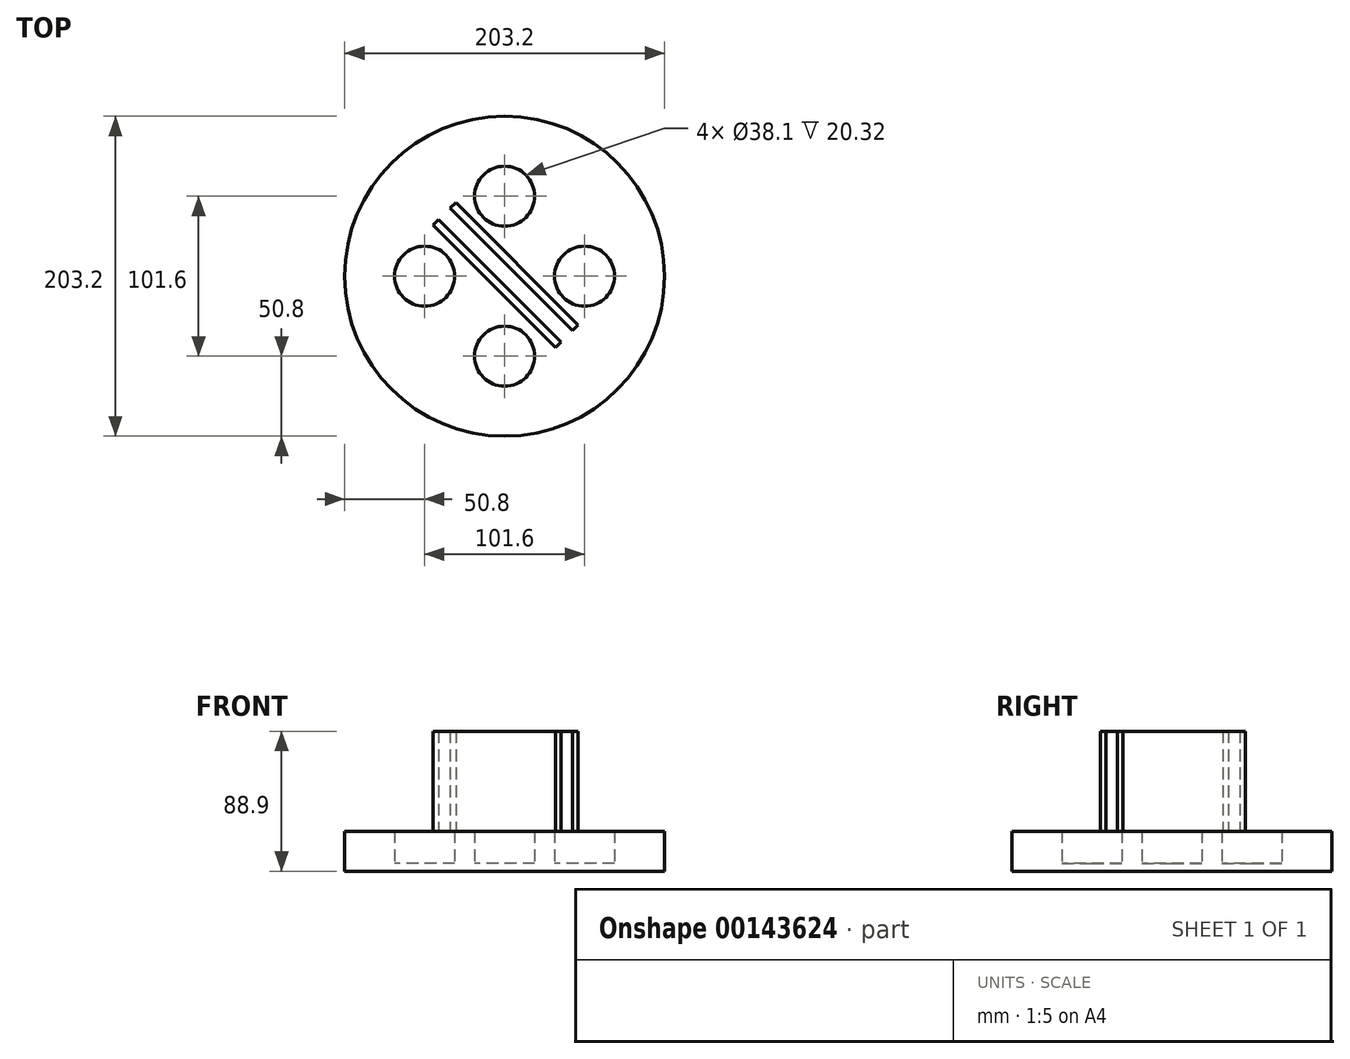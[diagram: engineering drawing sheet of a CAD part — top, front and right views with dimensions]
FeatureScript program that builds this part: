
annotation { "Feature Type Name" : "Feature", "Feature Type Description" : "" }
export const myFeature = defineFeature(function(context is Context, id is Id, definition is map)
    precondition{}
    {
        {
            var Q0;
            Q0=qCreatedBy(makeId("Top.planeOp"),FACE);
            var sketch = newSketch(context, id + "F0", { "sketchPlane" : qUnion([Q0])});
            skCircle(sketch, "E0", {"center": v(0, 0) * mm, "radius": 101.6 * mm});
            skLineSegment(sketch, "E1", {"start": v(0, 0) * mm, "end": v(-50.8, 0) * mm});
            skLineSegment(sketch, "E2", {"start": v(0, 0) * mm, "end": v(0, 50.8) * mm});
            skLineSegment(sketch, "E3", {"start": v(0, 0) * mm, "end": v(0, -50.8) * mm});
            skLineSegment(sketch, "E4", {"start": v(0, 0) * mm, "end": v(50.8, 0) * mm});
            skCircle(sketch, "E5", {"center": v(-50.8, 0) * mm, "radius": 19.05 * mm});
            skCircle(sketch, "E6", {"center": v(0, 50.8) * mm, "radius": 19.05 * mm});
            skCircle(sketch, "E7", {"center": v(50.8, 0) * mm, "radius": 19.05 * mm});
            skCircle(sketch, "E8", {"center": v(0, -50.8) * mm, "radius": 19.05 * mm});
            skSolve(sketch);
        }
        {
            var Q0;
            Q0 = qSketchRegion(id + "F0", true);
            extrude(context, id + "F1", {"entities" : qUnion([Q0]), "depth" : 25.4 * mm});
        }
        {
            var Q0;
            Q0=qCreatedBy(makeId("Top.planeOp"),FACE);
            var sketch = newSketch(context, id + "F2", { "sketchPlane" : qUnion([Q0])});
            skCircle(sketch, "E9", {"center": v(-50.8, 0) * mm, "radius": 19.05 * mm});
            skCircle(sketch, "E10", {"center": v(0, -50.8) * mm, "radius": 19.05 * mm});
            skCircle(sketch, "E11", {"center": v(0, 50.8) * mm, "radius": 19.05 * mm});
            skCircle(sketch, "E12", {"center": v(50.8, 0) * mm, "radius": 19.05 * mm});
            skSolve(sketch);
        }
        {
            var Q0;
            Q0 = qSketchRegion(id + "F2", true);
            extrude(context, id + "F3", {"entities" : qUnion([Q0]), "operationType" : NewBodyOperationType.ADD, "depth" : 5.08 * mm});
        }
        {
            var Q0;
            Q0=makeQuery(id+"F1.opExtrude","CAP_FACE",FACE,{"disambiguationData":[OSD([sQuery(id+"F0.wireOp",EDGE,"E0"),sQuery(id+"F0.wireOp",EDGE,"E5"),sQuery(id+"F0.wireOp",EDGE,"E6"),sQuery(id+"F0.wireOp",EDGE,"E7"),sQuery(id+"F0.wireOp",EDGE,"E8")])],"isStart":false});
            var sketch = newSketch(context, id + "F4", { "sketchPlane" : qUnion([Q0])});
            skLineSegment(sketch, "E13", {"start": v(-31.94, 18.86) * mm, "end": v(32.33, -45.41) * mm});
            skLineSegment(sketch, "E14", {"start": v(32.33, -45.41) * mm, "end": v(35.92, -41.82) * mm});
            skLineSegment(sketch, "E15", {"start": v(35.92, -41.82) * mm, "end": v(-41.82, 35.92) * mm});
            skLineSegment(sketch, "E16", {"start": v(-41.82, 35.92) * mm, "end": v(-45.41, 32.33) * mm});
            skLineSegment(sketch, "E17", {"start": v(-45.41, 32.33) * mm, "end": v(-31.94, 18.86) * mm});
            skLineSegment(sketch, "E18", {"start": v(-18.57, 34.32) * mm, "end": v(46.75, -31) * mm});
            skLineSegment(sketch, "E19", {"start": v(46.75, -31) * mm, "end": v(43.16, -34.58) * mm});
            skLineSegment(sketch, "E20", {"start": v(43.16, -34.58) * mm, "end": v(-34.58, 43.16) * mm});
            skLineSegment(sketch, "E21", {"start": v(-34.58, 43.16) * mm, "end": v(-31, 46.75) * mm});
            skLineSegment(sketch, "E22", {"start": v(-31, 46.75) * mm, "end": v(-18.57, 34.32) * mm});
            skSolve(sketch);
        }
        {
            var Q0;
            Q0 = qSketchRegion(id + "F4", true);
            extrude(context, id + "F5", {"entities" : qUnion([Q0]), "operationType" : NewBodyOperationType.ADD, "depth" : 63.5 * mm});
        }
    });
